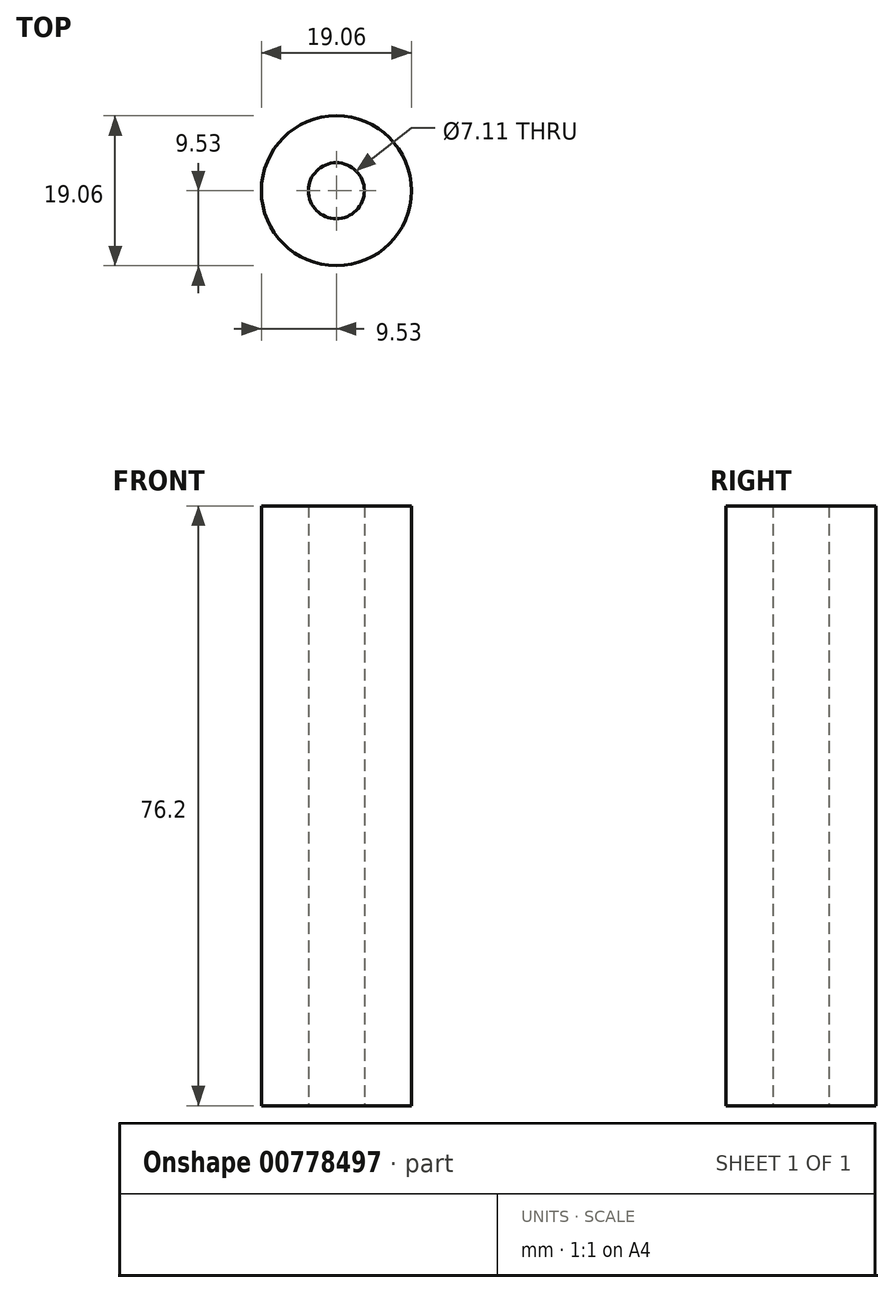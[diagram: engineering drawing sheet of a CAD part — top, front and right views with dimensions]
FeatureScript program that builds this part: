
annotation { "Feature Type Name" : "Feature", "Feature Type Description" : "" }
export const myFeature = defineFeature(function(context is Context, id is Id, definition is map)
    precondition{}
    {
        {
            var Q0;
            Q0=qCreatedBy(makeId("Top.planeOp"),FACE);
            var sketch = newSketch(context, id + "F0", { "sketchPlane" : qUnion([Q0])});
            skCircle(sketch, "E0", {"center": v(0, 0) * mm, "radius": 3.56 * mm});
            skCircle(sketch, "E1", {"center": v(0, 0) * mm, "radius": 9.53 * mm});
            skSolve(sketch);
        }
        {
            var Q0;
            Q0 = qSketchRegion(id + "F0", true);
            extrude(context, id + "F1", {"entities" : qUnion([Q0]), "depth" : 76.2 * mm, "offsetDistance" : 25.4 * mm});
        }
    });
